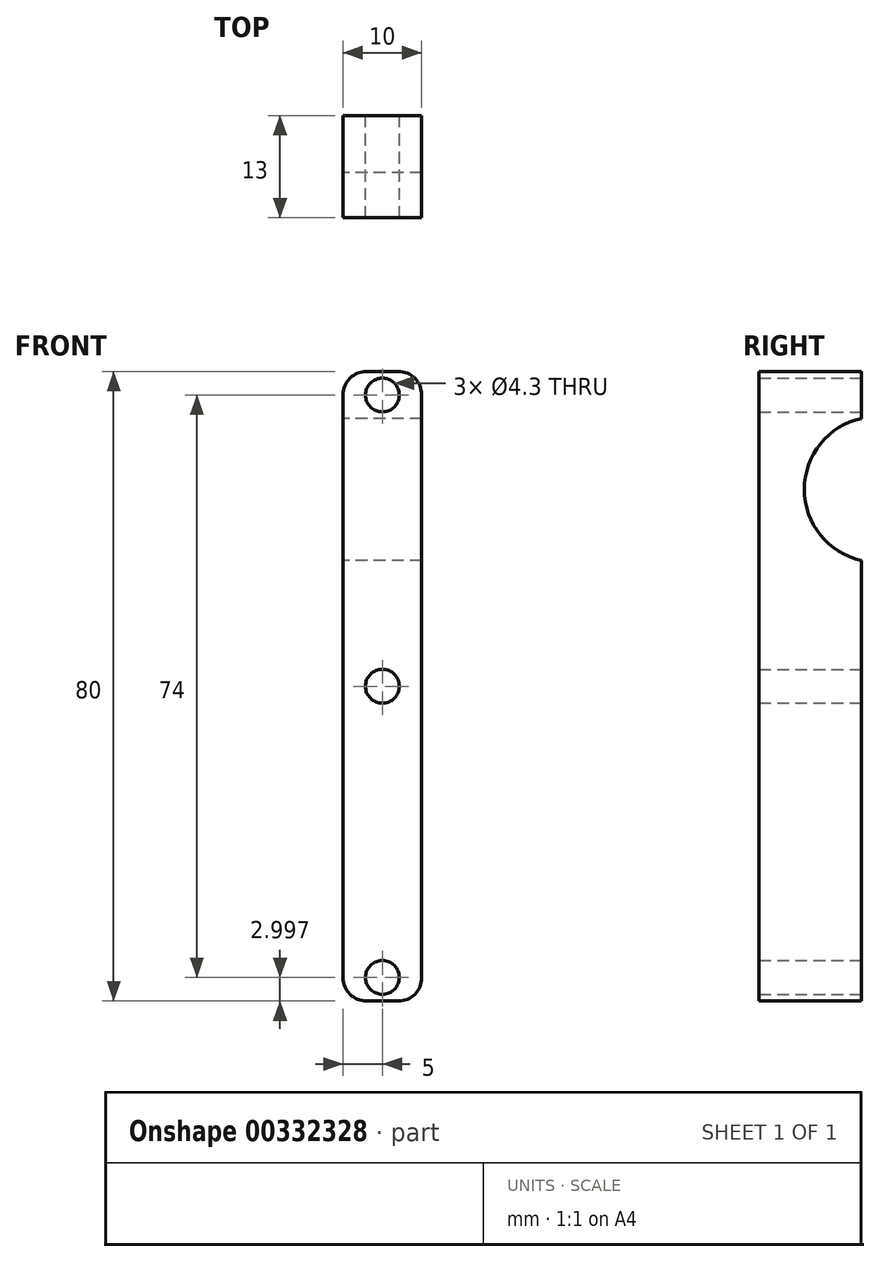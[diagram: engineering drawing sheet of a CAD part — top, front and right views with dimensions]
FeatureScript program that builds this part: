
annotation { "Feature Type Name" : "Feature", "Feature Type Description" : "" }
export const myFeature = defineFeature(function(context is Context, id is Id, definition is map)
    precondition{}
    {
        {
            var Q0;
            Q0=qCreatedBy(makeId("Front.planeOp"),FACE);
            var sketch = newSketch(context, id + "F0", { "sketchPlane" : qUnion([Q0])});
            skLineSegment(sketch, "E0.bottom", {"start": v(-2, 38.99) * mm, "end": v(2, 38.99) * mm});
            skLineSegment(sketch, "E0.top", {"start": v(-2, -41.01) * mm, "end": v(2, -41.01) * mm});
            skLineSegment(sketch, "E0.left", {"start": v(-5, 35.99) * mm, "end": v(-5, -38.01) * mm});
            skLineSegment(sketch, "E0.right", {"start": v(5, 35.99) * mm, "end": v(5, -38.01) * mm});
            skPoint(sketch, "E0.middle", {"position": v(0, -1.01) * mm});
            skPoint(sketch, "E1.visualSharp", {"position": v(-5, 38.99) * mm});
            skArc(sketch, "E1.filletArc", {"start": v(-2, 38.99) * mm, "mid": v(-4.12, 38.1) * mm, "end": v(-5, 35.99) * mm});
            skPoint(sketch, "E2.visualSharp", {"position": v(5, 38.99) * mm});
            skArc(sketch, "E2.filletArc", {"start": v(5, 35.99) * mm, "mid": v(4.12, 38.1) * mm, "end": v(2, 38.99) * mm});
            skPoint(sketch, "E3.visualSharp", {"position": v(5, -41.01) * mm});
            skArc(sketch, "E3.filletArc", {"start": v(2, -41.01) * mm, "mid": v(4.12, -40.13) * mm, "end": v(5, -38.01) * mm});
            skPoint(sketch, "E4.visualSharp", {"position": v(-5, -41.01) * mm});
            skArc(sketch, "E4.filletArc", {"start": v(-5, -38.01) * mm, "mid": v(-4.12, -40.13) * mm, "end": v(-2, -41.01) * mm});
            skLineSegment(sketch, "E5", {"start": v(0, -40.13) * mm, "end": v(0, 38.99) * mm, "construction": true});
            skPoint(sketch, "E5.startSnap0", {"position": v(0, -41.01) * mm});
            skPoint(sketch, "E5.startSnap1", {"position": v(4.12, -40.13) * mm});
            skPoint(sketch, "E6", {"position": v(0, -38.01) * mm});
            skPoint(sketch, "E7", {"position": v(0, 35.99) * mm});
            skCircle(sketch, "E8", {"center": v(0, -1.01) * mm, "radius": 2.15 * mm});
            skCircle(sketch, "E9", {"center": v(0, -38.01) * mm, "radius": 2.15 * mm});
            skCircle(sketch, "E10", {"center": v(0, 35.99) * mm, "radius": 2.15 * mm});
            skSolve(sketch);
        }
        {
            var Q0;
            Q0=makeQuery(id+"F0.imprint","IMPRINT",FACE,{"disambiguationData":[TD([[makeQuery(id+"F0.imprint","IMPRINT",EDGE,{"derivedFrom":sQuery(id+"F0.wireOp",EDGE,"E0.bottom")}),-1.0]])]});
            extrude(context, id + "F1", {"entities" : qUnion([Q0]), "depth" : 13 * mm});
        }
        {
            var Q0;
            Q0=makeQuery(id+"F1.opExtrude","SWEPT_FACE",FACE,{"disambiguationData":[OSD([sQuery(id+"F0.wireOp",EDGE,"E0.left")])]});
            var sketch = newSketch(context, id + "F2", { "sketchPlane" : qUnion([Q0])});
            skPoint(sketch, "E11", {"position": v(0, 23.99) * mm});
            skLineSegment(sketch, "E12", {"start": v(0, 23.99) * mm, "end": v(-2, 23.99) * mm});
            skCircle(sketch, "E13", {"center": v(-2, 23.99) * mm, "radius": 9.25 * mm});
            skLineSegment(sketch, "E14", {"start": v(13, -1.01) * mm, "end": v(0, -1.01) * mm});
            skCircle(sketch, "E15.MirrorC", {"center": v(-2, -26.01) * mm, "radius": 9.25 * mm});
            skSolve(sketch);
        }
        {
            var Q0;
            {var subQ1=makeQuery(id+"F1.opExtrude","CAP_EDGE",EDGE,{"disambiguationData":[OSD([sQuery(id+"F0.wireOp",EDGE,"E0.left")])],"isStart":true});var subQ4=makeQuery(id+"F2.imprint","IMPRINT",VERTEX,{"derivedFrom":subQ1});Q0=makeQuery(id+"F2.imprint","IMPRINT",FACE,{"disambiguationData":[TD([[makeQuery(id+"F2.imprint","IMPRINT",EDGE,{"disambiguationData":[TD([[subQ4,1.0]])],"derivedFrom":subQ1}),1.0]])]});}
            var Q1;
            {var subQ0=sQuery(id+"F2.wireOp",EDGE,"3775639f-127b-4948-a589-83142b340d380.MirrorC");var subQ1=makeQuery(id+"F1.opExtrude","CAP_EDGE",EDGE,{"disambiguationData":[OSD([sQuery(id+"F0.wireOp",EDGE,"E0.left")])],"isStart":true});var subQ2=makeQuery(id+"F2.imprint","INTERSECT",VERTEX,{"disambiguationData":[OD(0.0)],"derivedFrom":[subQ1,subQ0]});Q1=makeQuery(id+"F2.imprint","IMPRINT",FACE,{"disambiguationData":[TD([[makeQuery(id+"F2.imprint","IMPRINT",EDGE,{"disambiguationData":[TD([[subQ2,1.0]])],"derivedFrom":subQ0}),-1.0]])]});}
            var Q2;
            {var subQ0=sQuery(id+"F2.wireOp",EDGE,"E15.MirrorC");var subQ1=makeQuery(id+"F1.opExtrude","CAP_EDGE",EDGE,{"disambiguationData":[OSD([sQuery(id+"F0.wireOp",EDGE,"E0.left")])],"isStart":true});var subQ2=makeQuery(id+"F2.imprint","INTERSECT",VERTEX,{"disambiguationData":[OD(0.0)],"derivedFrom":[subQ1,subQ0]});Q2=makeQuery(id+"F2.imprint","IMPRINT",FACE,{"disambiguationData":[TD([[makeQuery(id+"F2.imprint","IMPRINT",EDGE,{"disambiguationData":[TD([[subQ2,1.0]])],"derivedFrom":subQ0}),-1.0]])]});}
            extrude(context, id + "F3", {"entities" : qUnion([Q0, Q1, Q2]), "operationType" : NewBodyOperationType.REMOVE, "oppositeDirection" : true, "depth" : 25 * mm});
        }
    });
